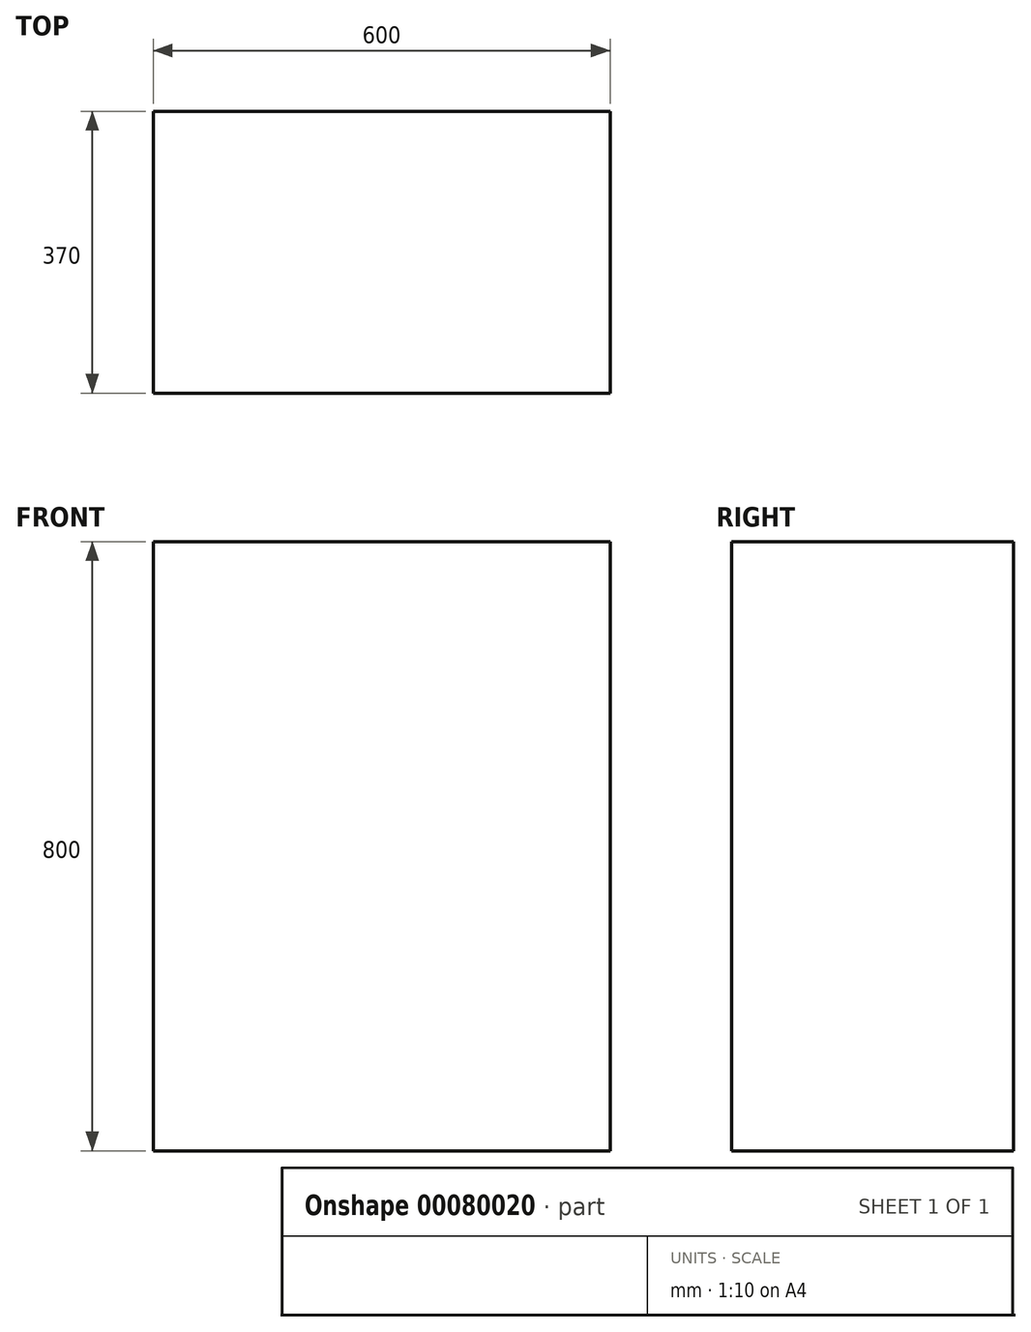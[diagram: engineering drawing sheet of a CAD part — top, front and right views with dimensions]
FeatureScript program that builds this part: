
annotation { "Feature Type Name" : "Feature", "Feature Type Description" : "" }
export const myFeature = defineFeature(function(context is Context, id is Id, definition is map)
    precondition{}
    {
        {
            var Q0;
            Q0=qCreatedBy(makeId("Top.planeOp"),FACE);
            var sketch = newSketch(context, id + "F0", { "sketchPlane" : qUnion([Q0])});
            skLineSegment(sketch, "E0.bottom", {"start": v(0, 0) * mm, "end": v(600, 0) * mm});
            skLineSegment(sketch, "E0.top", {"start": v(0, -370) * mm, "end": v(600, -370) * mm});
            skLineSegment(sketch, "E0.left", {"start": v(0, 0) * mm, "end": v(0, -370) * mm});
            skLineSegment(sketch, "E0.right", {"start": v(600, 0) * mm, "end": v(600, -370) * mm});
            skSolve(sketch);
        }
        {
            var Q0;
            Q0=makeQuery(id+"F0.imprint","IMPRINT",FACE,{"disambiguationData":[TD([[makeQuery(id+"F0.imprint","IMPRINT",EDGE,{"derivedFrom":sQuery(id+"F0.wireOp",EDGE,"E0.bottom")}),-1.0]])]});
            extrude(context, id + "F1", {"entities" : qUnion([Q0]), "depth" : 800 * mm});
        }
    });
